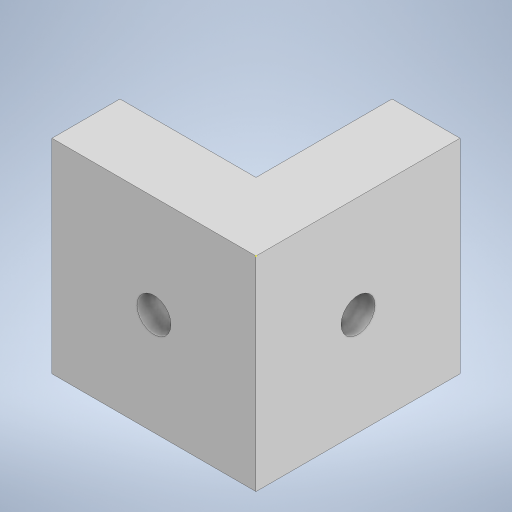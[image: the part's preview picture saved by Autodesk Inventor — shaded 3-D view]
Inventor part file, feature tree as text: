
AUTODESK INVENTOR PART (.ipt)
format: ipt  version: 2023 (Build 270158000, 158)  size: 224,256 bytes
history: native  units: mm
features: sketch x8, extrude x6
ambient origin geometry x8: Origin, YZ Plane, XZ Plane, XY Plane, X Axis, Y Axis, Z Axis, Center Point
bodies: Body1 (feature_tree)
feature tree (14):
  extrude  "Extrusion25"  Depth=30.0mm
  extrude  "Extrusion26"  Depth=30.0mm
  extrude  "Extrusion27"  Depth=10.0mm TaperAngle=0.0deg
  sketch  "Sketch37"  dims[d120=5.0mm d121=10.0mm d122=0.0mm]
  extrude  "Extrusion28"  Depth=10.0mm TaperAngle=0.0deg
  sketch  "Sketch39"  dims[d132=8.0mm d133=5.0mm d134=0.0mm]
  extrude  "Extrusion31"  Depth=10.0mm TaperAngle=0.0deg
  extrude  "Extrusion32"  Depth=5.0mm TaperAngle=0.0deg
  sketch  "Sketch34"  dims[d112=30.0mm d113=30.0mm]
  sketch  "Sketch35"  dims[d114=10.0mm d115=0.0mm d116=30.0mm]
  sketch  "Sketch36"  dims[d117=30.0mm d118=10.0mm d119=0.0mm]
  sketch  "Sketch38"  dims[d123=5.0mm d124=10.0mm d125=0.0mm]
  sketch  "Sketch42"  dims[d135=8.0mm]
  sketch  "Sketch43"  dims[d136=5.0mm d137=0.0mm d49=0.5mm d50=0.872665mm d51=0.5mm d52=0.872665mm d130=0.5mm d131=0.872665mm]
